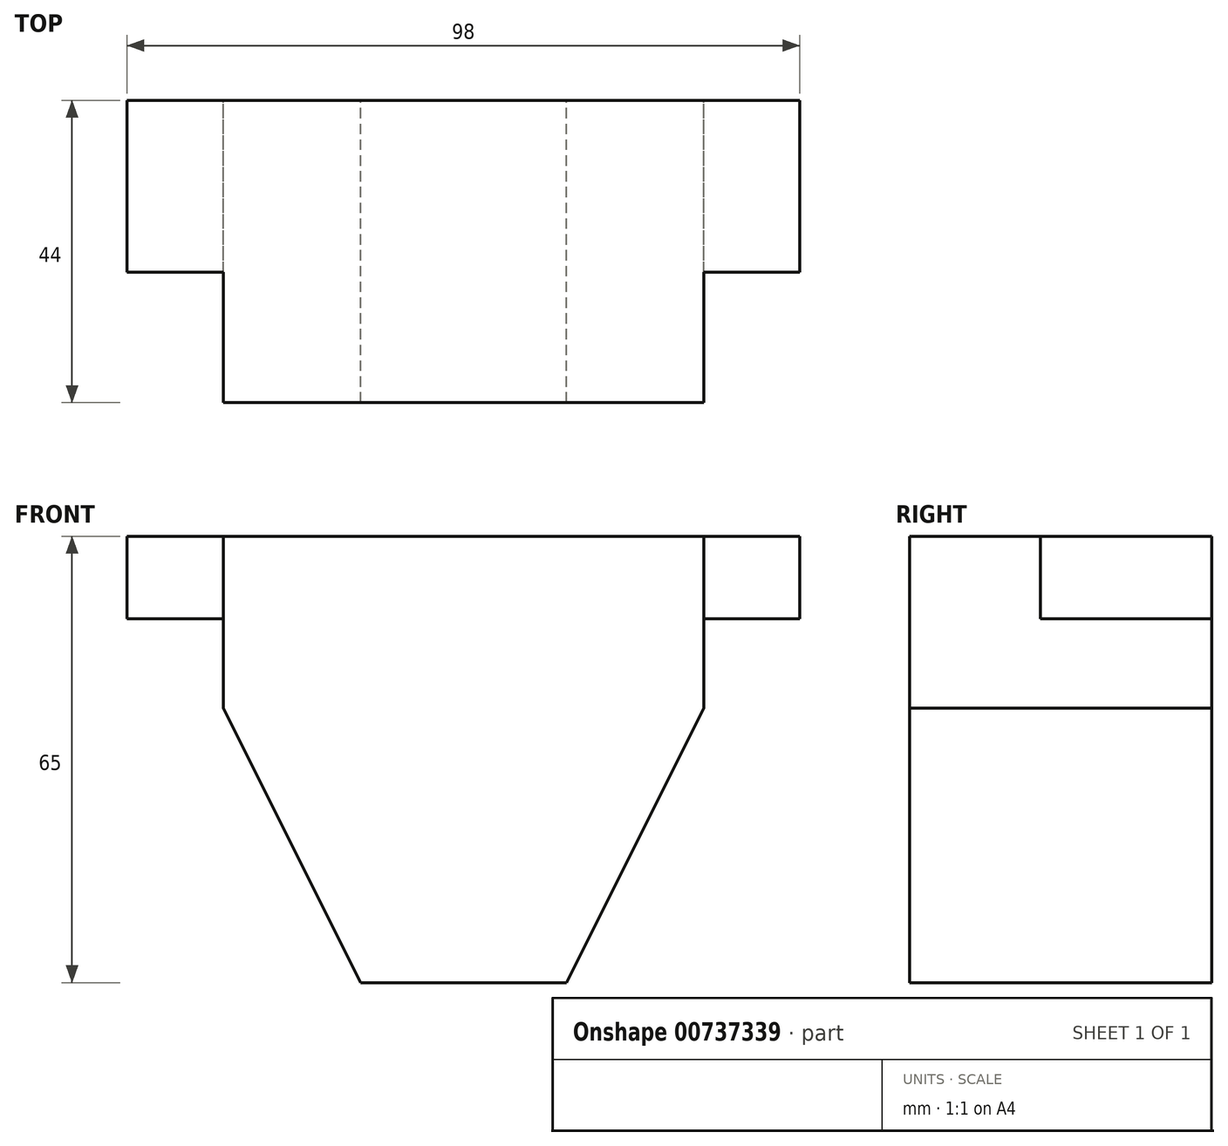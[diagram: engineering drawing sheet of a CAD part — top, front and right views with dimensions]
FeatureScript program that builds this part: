
annotation { "Feature Type Name" : "Feature", "Feature Type Description" : "" }
export const myFeature = defineFeature(function(context is Context, id is Id, definition is map)
    precondition{}
    {
        {
            var Q0;
            Q0=qCreatedBy(makeId("Front.planeOp"),FACE);
            var sketch = newSketch(context, id + "F0", { "sketchPlane" : qUnion([Q0])});
            skLineSegment(sketch, "E0.bottom", {"start": v(15, -32.5) * mm, "end": v(-15, -32.5) * mm});
            skLineSegment(sketch, "E0.top", {"start": v(35, 32.5) * mm, "end": v(-35, 32.5) * mm});
            skLineSegment(sketch, "E0.left", {"start": v(35, 7.5) * mm, "end": v(35, 20.5) * mm});
            skLineSegment(sketch, "E0.right", {"start": v(-35, 7.5) * mm, "end": v(-35, 20.5) * mm});
            skPoint(sketch, "E0.middle", {"position": v(0, 0) * mm});
            skLineSegment(sketch, "E1", {"start": v(-35, 20.5) * mm, "end": v(-49, 20.5) * mm});
            skLineSegment(sketch, "E2", {"start": v(-49, 20.5) * mm, "end": v(-49, 32.5) * mm});
            skLineSegment(sketch, "E3", {"start": v(-49, 32.5) * mm, "end": v(-35, 32.5) * mm});
            skLineSegment(sketch, "E4", {"start": v(35, 32.5) * mm, "end": v(49, 32.5) * mm});
            skLineSegment(sketch, "E5", {"start": v(49, 32.5) * mm, "end": v(49, 20.5) * mm});
            skLineSegment(sketch, "E6", {"start": v(49, 20.5) * mm, "end": v(35, 20.5) * mm});
            skLineSegment(sketch, "E7", {"start": v(-35, 7.5) * mm, "end": v(-15, -32.5) * mm});
            skLineSegment(sketch, "E8", {"start": v(35, 7.5) * mm, "end": v(15, -32.5) * mm});
            skLineSegment(sketch, "E9", {"start": v(-35, 32.5) * mm, "end": v(-35, 20.5) * mm});
            skLineSegment(sketch, "E10", {"start": v(35, 32.5) * mm, "end": v(35, 20.5) * mm});
            skPoint(sketch, "E11.orphan", {"position": v(-35, -32.5) * mm});
            skPoint(sketch, "E12.orphan", {"position": v(35, -32.5) * mm});
            skSolve(sketch);
        }
        {
            var Q0;
            Q0 = qSketchRegion(id + "F0", true);
            extrude(context, id + "F1", {"entities" : qUnion([Q0]), "depth" : 44 * mm, "offsetDistance" : 25 * mm});
        }
        {
            var Q0;
            Q0=makeQuery(id+"F1.opExtrude","CAP_FACE",FACE,{"disambiguationData":[OSD([sQuery(id+"F0.wireOp",EDGE,"E0.bottom"),sQuery(id+"F0.wireOp",EDGE,"E0.top"),sQuery(id+"F0.wireOp",EDGE,"E0.left"),sQuery(id+"F0.wireOp",EDGE,"E0.right"),sQuery(id+"F0.wireOp",EDGE,"E1"),sQuery(id+"F0.wireOp",EDGE,"E2"),sQuery(id+"F0.wireOp",EDGE,"E3"),sQuery(id+"F0.wireOp",EDGE,"E4"),sQuery(id+"F0.wireOp",EDGE,"E5"),sQuery(id+"F0.wireOp",EDGE,"E6"),sQuery(id+"F0.wireOp",EDGE,"E7"),sQuery(id+"F0.wireOp",EDGE,"E8")])],"isStart":false});
            var sketch = newSketch(context, id + "F2", { "sketchPlane" : qUnion([Q0])});
            skLineSegment(sketch, "E13", {"start": v(-35, 32.5) * mm, "end": v(-35, 20.5) * mm});
            skLineSegment(sketch, "E14", {"start": v(35, 32.5) * mm, "end": v(35, 20.5) * mm});
            skSolve(sketch);
        }
        {
            var Q0;
            {var subQ0=sQuery(id+"F2.wireOp",EDGE,"E13");Q0=makeQuery(id+"F2.imprint","IMPRINT",FACE,{"disambiguationData":[TD([[makeQuery(id+"F2.imprint","IMPRINT",EDGE,{"derivedFrom":subQ0}),-1.0]])]});}
            var Q1;
            {var subQ0=sQuery(id+"F2.wireOp",EDGE,"E14");Q1=makeQuery(id+"F2.imprint","IMPRINT",FACE,{"disambiguationData":[TD([[makeQuery(id+"F2.imprint","IMPRINT",EDGE,{"derivedFrom":subQ0}),1.0]])]});}
            extrude(context, id + "F3", {"entities" : qUnion([Q0, Q1]), "operationType" : NewBodyOperationType.REMOVE, "oppositeDirection" : true, "depth" : 19 * mm, "offsetDistance" : 25 * mm});
        }
    });
